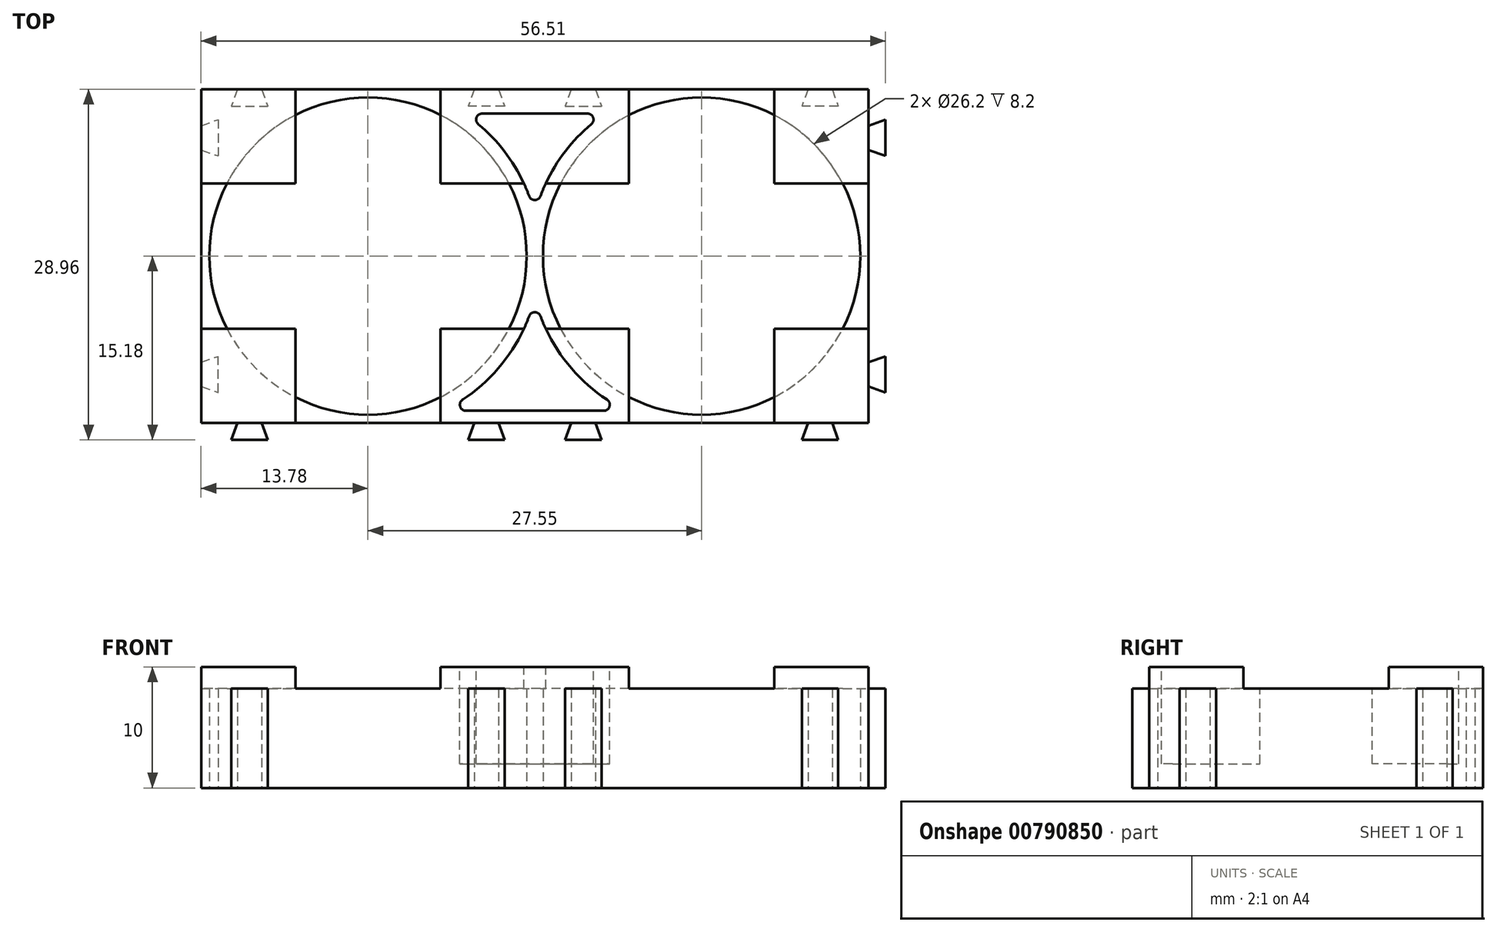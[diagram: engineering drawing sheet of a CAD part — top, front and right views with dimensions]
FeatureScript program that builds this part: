
annotation { "Feature Type Name" : "Feature", "Feature Type Description" : "" }
export const myFeature = defineFeature(function(context is Context, id is Id, definition is map)
    precondition{}
    {
        {
            var Q0;
            Q0=qCreatedBy(makeId("Top.planeOp"),FACE);
            var sketch = newSketch(context, id + "F0", { "sketchPlane" : qUnion([Q0])});
            skLineSegment(sketch, "E0.bottom", {"start": v(13.77, 13.78) * mm, "end": v(-13.77, 13.78) * mm});
            skLineSegment(sketch, "E0.top", {"start": v(13.78, -13.78) * mm, "end": v(-13.78, -13.78) * mm});
            skLineSegment(sketch, "E0.left", {"start": v(13.78, 13.78) * mm, "end": v(13.78, -13.78) * mm});
            skLineSegment(sketch, "E0.right", {"start": v(-13.78, 13.78) * mm, "end": v(-13.78, -13.78) * mm});
            skPoint(sketch, "E0.middle", {"position": v(0, 0) * mm});
            skCircle(sketch, "E1", {"center": v(0, 0) * mm, "radius": 13.1 * mm});
            skLineSegment(sketch, "E2", {"start": v(-11.28, 12.38) * mm, "end": v(-8.28, 12.38) * mm});
            skLineSegment(sketch, "E3", {"start": v(0, -13.78) * mm, "end": v(0, 13.78) * mm});
            skLineSegment(sketch, "E4", {"start": v(13.78, 0) * mm, "end": v(-13.78, 0) * mm});
            skLineSegment(sketch, "E5", {"start": v(-13.77, 13.78) * mm, "end": v(13.77, -13.78) * mm});
            skLineSegment(sketch, "E6", {"start": v(-9.78, 12.38) * mm, "end": v(-9.78, 13.78) * mm});
            skLineSegment(sketch, "E7", {"start": v(-9.78, 13.78) * mm, "end": v(-8.78, 13.78) * mm});
            skLineSegment(sketch, "E8", {"start": v(-8.78, 13.78) * mm, "end": v(-8.28, 12.38) * mm});
            skLineSegment(sketch, "E9.MirrorCS", {"start": v(-10.77, 13.78) * mm, "end": v(-11.28, 12.38) * mm});
            skLineSegment(sketch, "E10.MirrorCS", {"start": v(10.77, 13.78) * mm, "end": v(11.28, 12.38) * mm});
            skLineSegment(sketch, "E11.MirrorCS", {"start": v(11.28, 12.38) * mm, "end": v(8.28, 12.38) * mm});
            skLineSegment(sketch, "E12.MirrorCS", {"start": v(8.78, 13.78) * mm, "end": v(8.28, 12.38) * mm});
            skLineSegment(sketch, "E13.MirrorCS", {"start": v(-13.77, 10.78) * mm, "end": v(-12.37, 11.28) * mm});
            skLineSegment(sketch, "E14.MirrorCS", {"start": v(-12.37, 11.28) * mm, "end": v(-12.37, 8.28) * mm});
            skLineSegment(sketch, "E15.MirrorCS", {"start": v(-13.78, 8.78) * mm, "end": v(-12.37, 8.28) * mm});
            skLineSegment(sketch, "E16.MirrorCS", {"start": v(-13.77, -8.78) * mm, "end": v(-12.38, -8.28) * mm});
            skLineSegment(sketch, "E17.MirrorCS", {"start": v(-12.37, -11.27) * mm, "end": v(-12.37, -8.28) * mm});
            skLineSegment(sketch, "E18.MirrorCS", {"start": v(-13.78, -10.77) * mm, "end": v(-12.38, -11.27) * mm});
            skLineSegment(sketch, "E19", {"start": v(-11.28, -15.18) * mm, "end": v(-8.27, -15.18) * mm});
            skLineSegment(sketch, "E20", {"start": v(-10.77, -13.78) * mm, "end": v(-8.78, -13.78) * mm});
            skLineSegment(sketch, "E21", {"start": v(-10.77, -13.78) * mm, "end": v(-11.28, -15.18) * mm});
            skLineSegment(sketch, "E22", {"start": v(-8.78, -13.78) * mm, "end": v(-8.27, -15.17) * mm});
            skLineSegment(sketch, "E23.MirrorCS", {"start": v(8.78, -13.78) * mm, "end": v(8.27, -15.17) * mm});
            skLineSegment(sketch, "E24.MirrorCS", {"start": v(11.28, -15.18) * mm, "end": v(8.27, -15.18) * mm});
            skLineSegment(sketch, "E25.MirrorCS", {"start": v(10.77, -13.78) * mm, "end": v(11.28, -15.18) * mm});
            skLineSegment(sketch, "E26.MirrorCS", {"start": v(13.78, -10.77) * mm, "end": v(15.18, -11.28) * mm});
            skLineSegment(sketch, "E27.MirrorCS", {"start": v(15.18, -11.28) * mm, "end": v(15.18, -8.27) * mm});
            skLineSegment(sketch, "E28.MirrorCS", {"start": v(13.78, -8.78) * mm, "end": v(15.17, -8.27) * mm});
            skLineSegment(sketch, "E29.MirrorCS", {"start": v(13.78, 8.78) * mm, "end": v(15.18, 8.27) * mm});
            skLineSegment(sketch, "E30.MirrorCS", {"start": v(15.18, 11.27) * mm, "end": v(15.18, 8.27) * mm});
            skLineSegment(sketch, "E31.MirrorCS", {"start": v(13.78, 10.77) * mm, "end": v(15.18, 11.27) * mm});
            skLineSegment(sketch, "E32.1.0.0", {"start": v(38.82, -15.18) * mm, "end": v(35.82, -15.18) * mm});
            skLineSegment(sketch, "E32.1.0.1", {"start": v(41.33, 13.78) * mm, "end": v(13.78, 13.78) * mm});
            skLineSegment(sketch, "E32.1.0.2", {"start": v(41.33, -13.78) * mm, "end": v(13.78, -13.78) * mm});
            skLineSegment(sketch, "E32.1.0.3", {"start": v(41.33, 13.78) * mm, "end": v(41.33, -13.78) * mm});
            skLineSegment(sketch, "E32.1.0.4", {"start": v(13.77, 13.78) * mm, "end": v(13.77, -13.78) * mm});
            skPoint(sketch, "E32.1.0.5", {"position": v(27.55, 0) * mm});
            skLineSegment(sketch, "E32.1.0.6", {"start": v(27.55, -13.78) * mm, "end": v(27.55, 13.78) * mm});
            skLineSegment(sketch, "E32.1.0.8", {"start": v(16.28, -15.18) * mm, "end": v(19.28, -15.18) * mm});
            skLineSegment(sketch, "E32.1.0.9", {"start": v(41.33, 0) * mm, "end": v(13.78, 0) * mm});
            skLineSegment(sketch, "E32.1.0.10", {"start": v(13.78, 13.78) * mm, "end": v(41.33, -13.77) * mm});
            skLineSegment(sketch, "E32.1.0.12", {"start": v(15.18, -11.27) * mm, "end": v(15.18, -8.28) * mm});
            skCircle(sketch, "E32.1.0.13", {"center": v(27.55, 0) * mm, "radius": 13.1 * mm});
            skLineSegment(sketch, "E32.1.0.14", {"start": v(15.18, 11.28) * mm, "end": v(15.18, 8.28) * mm});
            skLineSegment(sketch, "E32.1.0.15", {"start": v(38.82, 12.37) * mm, "end": v(35.83, 12.37) * mm});
            skLineSegment(sketch, "E32.1.0.16", {"start": v(38.32, -13.77) * mm, "end": v(38.83, -15.17) * mm});
            skLineSegment(sketch, "E32.1.0.17", {"start": v(36.33, -13.78) * mm, "end": v(35.83, -15.18) * mm});
            skLineSegment(sketch, "E32.1.0.18", {"start": v(16.28, 12.38) * mm, "end": v(19.27, 12.38) * mm});
            skLineSegment(sketch, "E32.1.0.19", {"start": v(13.77, -10.77) * mm, "end": v(15.18, -11.27) * mm});
            skLineSegment(sketch, "E32.1.0.20", {"start": v(17.77, 12.38) * mm, "end": v(17.77, 13.78) * mm});
            skLineSegment(sketch, "E32.1.0.21", {"start": v(13.78, -8.78) * mm, "end": v(15.18, -8.28) * mm});
            skLineSegment(sketch, "E32.1.0.22", {"start": v(13.78, 8.78) * mm, "end": v(15.18, 8.28) * mm});
            skLineSegment(sketch, "E32.1.0.23", {"start": v(38.32, 13.78) * mm, "end": v(38.82, 12.38) * mm});
            skLineSegment(sketch, "E32.1.0.24", {"start": v(13.78, 10.78) * mm, "end": v(15.18, 11.28) * mm});
            skLineSegment(sketch, "E32.1.0.25", {"start": v(36.33, 13.78) * mm, "end": v(35.83, 12.38) * mm});
            skLineSegment(sketch, "E32.1.0.26", {"start": v(18.77, -13.78) * mm, "end": v(19.28, -15.18) * mm});
            skLineSegment(sketch, "E32.1.0.27", {"start": v(16.78, -13.78) * mm, "end": v(16.28, -15.18) * mm});
            skLineSegment(sketch, "E32.1.0.28", {"start": v(16.78, -13.78) * mm, "end": v(18.77, -13.78) * mm});
            skLineSegment(sketch, "E32.1.0.29", {"start": v(17.77, 13.78) * mm, "end": v(18.77, 13.78) * mm});
            skLineSegment(sketch, "E32.1.0.30", {"start": v(18.77, 13.78) * mm, "end": v(19.27, 12.38) * mm});
            skLineSegment(sketch, "E32.1.0.31", {"start": v(16.78, 13.78) * mm, "end": v(16.27, 12.38) * mm});
            skLineSegment(sketch, "E32.1.0.32", {"start": v(42.73, 11.27) * mm, "end": v(42.73, 8.27) * mm});
            skLineSegment(sketch, "E32.1.0.33", {"start": v(41.33, 10.77) * mm, "end": v(42.73, 11.27) * mm});
            skLineSegment(sketch, "E32.1.0.34", {"start": v(41.33, 8.78) * mm, "end": v(42.73, 8.27) * mm});
            skLineSegment(sketch, "E32.1.0.35", {"start": v(41.33, -8.78) * mm, "end": v(42.73, -8.27) * mm});
            skLineSegment(sketch, "E32.1.0.36", {"start": v(42.73, -11.28) * mm, "end": v(42.73, -8.27) * mm});
            skLineSegment(sketch, "E32.1.0.37", {"start": v(41.33, -10.77) * mm, "end": v(42.73, -11.27) * mm});
            skLineSegment(sketch, "E32.direction1", {"start": v(-13.78, -13.78) * mm, "end": v(13.78, -13.78) * mm, "construction": true});
            skSolve(sketch);
        }
        {
            var Q0;
            {var subQ4=sQuery(id+"F0.wireOp",EDGE,"E10.MirrorCS");Q0=makeQuery(id+"F0.imprint","IMPRINT",FACE,{"disambiguationData":[TD([[makeQuery(id+"F0.imprint","IMPRINT",EDGE,{"derivedFrom":subQ4}),1.0]])]});}
            var Q1;
            {var subQ0=sQuery(id+"F0.wireOp",EDGE,"E29.MirrorCS");Q1=makeQuery(id+"F0.imprint","IMPRINT",FACE,{"disambiguationData":[TD([[makeQuery(id+"F0.imprint","IMPRINT",EDGE,{"derivedFrom":subQ0}),1.0]])]});}
            var Q2;
            {var subQ0=sQuery(id+"F0.wireOp",EDGE,"E26.MirrorCS");Q2=makeQuery(id+"F0.imprint","IMPRINT",FACE,{"disambiguationData":[TD([[makeQuery(id+"F0.imprint","IMPRINT",EDGE,{"derivedFrom":subQ0}),1.0]])]});}
            var Q3;
            {var subQ0=sQuery(id+"F0.wireOp",EDGE,"E4");var subQ5=sQuery(id+"F0.wireOp",EDGE,"E0.left");var subQ9=makeQuery(id+"F0.imprint","INTERSECT",VERTEX,{"derivedFrom":[subQ5,subQ0]});Q3=makeQuery(id+"F0.imprint","IMPRINT",FACE,{"disambiguationData":[TD([[makeQuery(id+"F0.imprint","IMPRINT",EDGE,{"disambiguationData":[TD([[subQ9,-1.0]])],"derivedFrom":subQ5}),-1.0]])]});}
            var Q4;
            {var subQ1=sQuery(id+"F0.wireOp",EDGE,"E0.top");var subQ3=makeQuery(id+"F0.imprint","INTERSECT",VERTEX,{"derivedFrom":[subQ1,sQuery(id+"F0.wireOp",EDGE,"E23.MirrorCS")]});Q4=makeQuery(id+"F0.imprint","IMPRINT",FACE,{"disambiguationData":[TD([[makeQuery(id+"F0.imprint","IMPRINT",EDGE,{"disambiguationData":[TD([[subQ3,1.0]])],"derivedFrom":subQ1}),-1.0]])]});}
            var Q5;
            {var subQ0=sQuery(id+"F0.wireOp",EDGE,"E23.MirrorCS");Q5=makeQuery(id+"F0.imprint","IMPRINT",FACE,{"disambiguationData":[TD([[makeQuery(id+"F0.imprint","IMPRINT",EDGE,{"derivedFrom":subQ0}),1.0]])]});}
            var Q6;
            {var subQ11=sQuery(id+"F0.wireOp",EDGE,"E16.MirrorCS");Q6=makeQuery(id+"F0.imprint","IMPRINT",FACE,{"disambiguationData":[TD([[makeQuery(id+"F0.imprint","IMPRINT",EDGE,{"derivedFrom":subQ11}),1.0]])]});}
            var Q7;
            Q7=makeQuery(id+"F0.imprint","IMPRINT",FACE,{"disambiguationData":[TD([[makeQuery(id+"F0.imprint","IMPRINT",EDGE,{"derivedFrom":sQuery(id+"F0.wireOp",EDGE,"E19")}),1.0]])]});
            var Q8;
            {var subQ9=sQuery(id+"F0.wireOp",EDGE,"E13.MirrorCS");Q8=makeQuery(id+"F0.imprint","IMPRINT",FACE,{"disambiguationData":[TD([[makeQuery(id+"F0.imprint","IMPRINT",EDGE,{"derivedFrom":subQ9}),1.0]])]});}
            var Q9;
            {var subQ11=sQuery(id+"F0.wireOp",EDGE,"E8");Q9=makeQuery(id+"F0.imprint","IMPRINT",FACE,{"disambiguationData":[TD([[makeQuery(id+"F0.imprint","IMPRINT",EDGE,{"derivedFrom":subQ11}),1.0]])]});}
            var Q10;
            {var subQ1=sQuery(id+"F0.wireOp",EDGE,"E4");var subQ4=sQuery(id+"F0.wireOp",EDGE,"E1");var subQ5=makeQuery(id+"F0.imprint","INTERSECT",VERTEX,{"disambiguationData":[OD(0.0)],"derivedFrom":[subQ4,subQ1]});Q10=makeQuery(id+"F0.imprint","IMPRINT",FACE,{"disambiguationData":[TD([[makeQuery(id+"F0.imprint","IMPRINT",EDGE,{"disambiguationData":[TD([[subQ5,1.0]])],"derivedFrom":subQ4}),-1.0]])]});}
            var Q11;
            Q11=makeQuery(id+"F0.imprint","IMPRINT",FACE,{"disambiguationData":[TD([[makeQuery(id+"F0.imprint","IMPRINT",EDGE,{"derivedFrom":sQuery(id+"F0.wireOp",EDGE,"E32.1.0.12")}),-1.0]])]});
            var Q12;
            Q12=makeQuery(id+"F0.imprint","IMPRINT",FACE,{"disambiguationData":[TD([[makeQuery(id+"F0.imprint","IMPRINT",EDGE,{"derivedFrom":sQuery(id+"F0.wireOp",EDGE,"E32.1.0.12")}),1.0]])]});
            var Q13;
            Q13=makeQuery(id+"F0.imprint","IMPRINT",FACE,{"disambiguationData":[TD([[makeQuery(id+"F0.imprint","IMPRINT",EDGE,{"derivedFrom":sQuery(id+"F0.wireOp",EDGE,"E32.1.0.14")}),-1.0]])]});
            var Q14;
            Q14=makeQuery(id+"F0.imprint","IMPRINT",FACE,{"disambiguationData":[TD([[makeQuery(id+"F0.imprint","IMPRINT",EDGE,{"derivedFrom":sQuery(id+"F0.wireOp",EDGE,"E32.1.0.14")}),1.0]])]});
            var Q15;
            {var subQ13=sQuery(id+"F0.wireOp",EDGE,"E32.1.0.30");Q15=makeQuery(id+"F0.imprint","IMPRINT",FACE,{"disambiguationData":[TD([[makeQuery(id+"F0.imprint","IMPRINT",EDGE,{"derivedFrom":subQ13}),1.0]])]});}
            var Q16;
            {var subQ1=sQuery(id+"F0.wireOp",EDGE,"E0.bottom");var subQ3=sQuery(id+"F0.wireOp",EDGE,"E32.1.0.7");var subQ4=makeQuery(id+"F0.imprint","INTERSECT",VERTEX,{"derivedFrom":[subQ1,subQ3]});Q16=makeQuery(id+"F0.imprint","IMPRINT",FACE,{"disambiguationData":[TD([[makeQuery(id+"F0.imprint","IMPRINT",EDGE,{"disambiguationData":[TD([[subQ4,1.0]])],"derivedFrom":subQ3}),-1.0]])]});}
            var Q17;
            {var subQ1=sQuery(id+"F0.wireOp",EDGE,"E32.1.0.4");var subQ3=sQuery(id+"F0.wireOp",EDGE,"E32.1.0.7");var subQ4=makeQuery(id+"F0.imprint","INTERSECT",VERTEX,{"derivedFrom":[subQ1,subQ3]});Q17=makeQuery(id+"F0.imprint","IMPRINT",FACE,{"disambiguationData":[TD([[makeQuery(id+"F0.imprint","IMPRINT",EDGE,{"disambiguationData":[TD([[subQ4,1.0]])],"derivedFrom":subQ3}),-1.0]])]});}
            var Q18;
            {var subQ1=sQuery(id+"F0.wireOp",EDGE,"E32.1.0.1");var subQ3=sQuery(id+"F0.wireOp",EDGE,"E32.1.0.7");var subQ4=makeQuery(id+"F0.imprint","INTERSECT",VERTEX,{"derivedFrom":[subQ1,subQ3]});Q18=makeQuery(id+"F0.imprint","IMPRINT",FACE,{"disambiguationData":[TD([[makeQuery(id+"F0.imprint","IMPRINT",EDGE,{"disambiguationData":[TD([[subQ4,-1.0]])],"derivedFrom":subQ3}),-1.0]])]});}
            var Q19;
            Q19=makeQuery(id+"F0.imprint","IMPRINT",FACE,{"disambiguationData":[TD([[makeQuery(id+"F0.imprint","IMPRINT",EDGE,{"derivedFrom":sQuery(id+"F0.wireOp",EDGE,"E32.1.0.15")}),1.0]])]});
            var Q20;
            Q20=makeQuery(id+"F0.imprint","IMPRINT",FACE,{"disambiguationData":[TD([[makeQuery(id+"F0.imprint","IMPRINT",EDGE,{"derivedFrom":sQuery(id+"F0.wireOp",EDGE,"E32.1.0.32")}),-1.0]])]});
            var Q21;
            Q21=makeQuery(id+"F0.imprint","IMPRINT",FACE,{"disambiguationData":[TD([[makeQuery(id+"F0.imprint","IMPRINT",EDGE,{"derivedFrom":sQuery(id+"F0.wireOp",EDGE,"E32.1.0.8")}),1.0]])]});
            var Q22;
            Q22=makeQuery(id+"F0.imprint","IMPRINT",FACE,{"disambiguationData":[TD([[makeQuery(id+"F0.imprint","IMPRINT",EDGE,{"derivedFrom":sQuery(id+"F0.wireOp",EDGE,"E32.1.0.0")}),-1.0]])]});
            var Q23;
            {var subQ0=sQuery(id+"F0.wireOp",EDGE,"E32.1.0.35");Q23=makeQuery(id+"F0.imprint","IMPRINT",FACE,{"disambiguationData":[TD([[makeQuery(id+"F0.imprint","IMPRINT",EDGE,{"derivedFrom":subQ0}),-1.0]])]});}
            var Q24;
            {var subQ1=sQuery(id+"F0.wireOp",EDGE,"E32.1.0.3");var subQ5=sQuery(id+"F0.wireOp",EDGE,"E32.1.0.9");var subQ6=makeQuery(id+"F0.imprint","INTERSECT",VERTEX,{"derivedFrom":[subQ1,subQ5]});Q24=makeQuery(id+"F0.imprint","IMPRINT",FACE,{"disambiguationData":[TD([[makeQuery(id+"F0.imprint","IMPRINT",EDGE,{"disambiguationData":[TD([[subQ6,-1.0]])],"derivedFrom":subQ1}),-1.0]])]});}
            var Q25;
            {var subQ1=sQuery(id+"F0.wireOp",EDGE,"E32.1.0.2");var subQ4=makeQuery(id+"F0.imprint","INTERSECT",VERTEX,{"derivedFrom":[subQ1,sQuery(id+"F0.wireOp",EDGE,"E32.1.0.16")]});Q25=makeQuery(id+"F0.imprint","IMPRINT",FACE,{"disambiguationData":[TD([[makeQuery(id+"F0.imprint","IMPRINT",EDGE,{"disambiguationData":[TD([[subQ4,-1.0]])],"derivedFrom":subQ1}),-1.0]])]});}
            extrude(context, id + "F1", {"entities" : qUnion([Q0, Q1, Q2, Q3, Q4, Q5, Q6, Q7, Q8, Q9, Q10, Q11, Q12, Q13, Q14, Q15, Q16, Q17, Q18, Q19, Q20, Q21, Q22, Q23, Q24, Q25]), "depth" : (10 - 1.8) * mm, "offsetDistance" : 25 * mm});
        }
        {
            var Q0;
            Q0=makeQuery(id+"F1.opExtrude","CAP_FACE",FACE,{"disambiguationData":[OSD([sQuery(id+"F0.wireOp",EDGE,"E0.bottom"),sQuery(id+"F0.wireOp",EDGE,"E0.top"),sQuery(id+"F0.wireOp",EDGE,"E0.left"),sQuery(id+"F0.wireOp",EDGE,"E0.right"),sQuery(id+"F0.wireOp",EDGE,"E1"),sQuery(id+"F0.wireOp",EDGE,"E2"),sQuery(id+"F0.wireOp",EDGE,"E8"),sQuery(id+"F0.wireOp",EDGE,"E9.MirrorCS"),sQuery(id+"F0.wireOp",EDGE,"E10.MirrorCS"),sQuery(id+"F0.wireOp",EDGE,"E11.MirrorCS"),sQuery(id+"F0.wireOp",EDGE,"E12.MirrorCS"),sQuery(id+"F0.wireOp",EDGE,"E13.MirrorCS"),sQuery(id+"F0.wireOp",EDGE,"E14.MirrorCS"),sQuery(id+"F0.wireOp",EDGE,"E15.MirrorCS"),sQuery(id+"F0.wireOp",EDGE,"E16.MirrorCS"),sQuery(id+"F0.wireOp",EDGE,"E17.MirrorCS"),sQuery(id+"F0.wireOp",EDGE,"E18.MirrorCS"),sQuery(id+"F0.wireOp",EDGE,"E19"),sQuery(id+"F0.wireOp",EDGE,"E21"),sQuery(id+"F0.wireOp",EDGE,"E22"),sQuery(id+"F0.wireOp",EDGE,"E23.MirrorCS"),sQuery(id+"F0.wireOp",EDGE,"E24.MirrorCS"),sQuery(id+"F0.wireOp",EDGE,"E25.MirrorCS"),sQuery(id+"F0.wireOp",EDGE,"E26.MirrorCS"),sQuery(id+"F0.wireOp",EDGE,"E27.MirrorCS"),sQuery(id+"F0.wireOp",EDGE,"E28.MirrorCS"),sQuery(id+"F0.wireOp",EDGE,"E29.MirrorCS"),sQuery(id+"F0.wireOp",EDGE,"E30.MirrorCS"),sQuery(id+"F0.wireOp",EDGE,"E31.MirrorCS")])],"isStart":false});
            var sketch = newSketch(context, id + "F2", { "sketchPlane" : qUnion([Q0])});
            skLineSegment(sketch, "E33", {"start": v(13.78, -13.78) * mm, "end": v(-13.78, 13.78) * mm});
            skLineSegment(sketch, "E34", {"start": v(13.78, 13.77) * mm, "end": v(-13.77, -13.78) * mm});
            skLineSegment(sketch, "E35", {"start": v(0, 0) * mm, "end": v(0, -13.77) * mm});
            skLineSegment(sketch, "E36", {"start": v(0, -13.78) * mm, "end": v(6, -13.78) * mm});
            skLineSegment(sketch, "E37", {"start": v(6, -13.78) * mm, "end": v(6, -6) * mm});
            skLineSegment(sketch, "E38", {"start": v(6, -6) * mm, "end": v(13.78, -6) * mm});
            skLineSegment(sketch, "E39", {"start": v(6, 6) * mm, "end": v(6, 13.77) * mm});
            skLineSegment(sketch, "E40", {"start": v(6, 6) * mm, "end": v(13.78, 6) * mm});
            skLineSegment(sketch, "E41", {"start": v(6, 13.77) * mm, "end": v(13.78, 13.77) * mm});
            skLineSegment(sketch, "E42", {"start": v(13.78, 6) * mm, "end": v(13.78, 13.77) * mm});
            skLineSegment(sketch, "E43", {"start": v(13.78, -6) * mm, "end": v(13.78, -13.78) * mm});
            skLineSegment(sketch, "E44", {"start": v(6, -13.78) * mm, "end": v(13.78, -13.78) * mm});
            skLineSegment(sketch, "E45", {"start": v(-6, 6) * mm, "end": v(-13.78, 6) * mm});
            skLineSegment(sketch, "E46", {"start": v(-6, 6) * mm, "end": v(-6, 13.78) * mm});
            skLineSegment(sketch, "E47", {"start": v(-6, 13.78) * mm, "end": v(-13.78, 13.78) * mm});
            skLineSegment(sketch, "E48", {"start": v(-13.78, 13.78) * mm, "end": v(-13.78, 6) * mm});
            skLineSegment(sketch, "E49", {"start": v(-6, -6) * mm, "end": v(-13.78, -6) * mm});
            skLineSegment(sketch, "E50", {"start": v(-6, -6) * mm, "end": v(-6, -13.78) * mm});
            skLineSegment(sketch, "E51", {"start": v(-6, -13.78) * mm, "end": v(-13.78, -13.78) * mm});
            skLineSegment(sketch, "E52", {"start": v(-13.78, -13.78) * mm, "end": v(-13.78, -6) * mm});
            skLineSegment(sketch, "E53.1.0.0", {"start": v(13.78, 13.78) * mm, "end": v(13.78, 6) * mm});
            skLineSegment(sketch, "E53.1.0.1", {"start": v(21.55, 13.78) * mm, "end": v(13.77, 13.78) * mm});
            skLineSegment(sketch, "E53.1.0.2", {"start": v(21.55, 6) * mm, "end": v(21.55, 13.78) * mm});
            skLineSegment(sketch, "E53.1.0.3", {"start": v(21.55, 6) * mm, "end": v(13.78, 6) * mm});
            skLineSegment(sketch, "E53.1.0.4", {"start": v(33.55, 6) * mm, "end": v(33.55, 13.78) * mm});
            skLineSegment(sketch, "E53.1.0.5", {"start": v(33.55, 13.78) * mm, "end": v(41.33, 13.78) * mm});
            skLineSegment(sketch, "E53.1.0.6", {"start": v(41.33, 6) * mm, "end": v(41.33, 13.78) * mm});
            skLineSegment(sketch, "E53.1.0.7", {"start": v(33.55, 6) * mm, "end": v(41.33, 6) * mm});
            skLineSegment(sketch, "E53.1.0.8", {"start": v(33.55, -6) * mm, "end": v(41.33, -6) * mm});
            skLineSegment(sketch, "E53.1.0.9", {"start": v(33.55, -13.78) * mm, "end": v(33.55, -6) * mm});
            skLineSegment(sketch, "E53.1.0.10", {"start": v(33.55, -13.78) * mm, "end": v(41.33, -13.78) * mm});
            skLineSegment(sketch, "E53.1.0.11", {"start": v(41.33, -6) * mm, "end": v(41.33, -13.78) * mm});
            skLineSegment(sketch, "E53.1.0.12", {"start": v(21.55, -6) * mm, "end": v(21.55, -13.78) * mm});
            skLineSegment(sketch, "E53.1.0.13", {"start": v(21.55, -6) * mm, "end": v(13.78, -6) * mm});
            skLineSegment(sketch, "E53.1.0.14", {"start": v(13.78, -13.78) * mm, "end": v(13.78, -6) * mm});
            skLineSegment(sketch, "E53.1.0.15", {"start": v(21.55, -13.77) * mm, "end": v(13.77, -13.77) * mm});
            skLineSegment(sketch, "E53.direction1", {"start": v(-13.78, 6) * mm, "end": v(13.78, 6) * mm, "construction": true});
            skSolve(sketch);
        }
        {
            var Q0;
            {var subQ1=makeQuery(id+"F1.opExtrude","CAP_EDGE",EDGE,{"disambiguationData":[OSD([sQuery(id+"F0.wireOp",EDGE,"E10.MirrorCS")])],"isStart":false});Q0=makeQuery(id+"F2.imprint","IMPRINT",FACE,{"disambiguationData":[TD([[makeQuery(id+"F2.imprint","IMPRINT",EDGE,{"derivedFrom":subQ1}),-1.0]])]});}
            var Q1;
            Q1=makeQuery(id+"F2.imprint","IMPRINT",FACE,{"disambiguationData":[TD([[makeQuery(id+"F2.imprint","IMPRINT",EDGE,{"derivedFrom":makeQuery(id+"F1.opExtrude","CAP_EDGE",EDGE,{"disambiguationData":[OSD([sQuery(id+"F0.wireOp",EDGE,"E2")])],"isStart":false})}),1.0]])]});
            var Q2;
            {var subQ1=makeQuery(id+"F1.opExtrude","CAP_EDGE",EDGE,{"disambiguationData":[OSD([sQuery(id+"F0.wireOp",EDGE,"E13.MirrorCS")])],"isStart":false});Q2=makeQuery(id+"F2.imprint","IMPRINT",FACE,{"disambiguationData":[TD([[makeQuery(id+"F2.imprint","IMPRINT",EDGE,{"derivedFrom":subQ1}),-1.0]])]});}
            var Q3;
            {var subQ1=makeQuery(id+"F1.opExtrude","CAP_EDGE",EDGE,{"disambiguationData":[OSD([sQuery(id+"F0.wireOp",EDGE,"E16.MirrorCS")])],"isStart":false});Q3=makeQuery(id+"F2.imprint","IMPRINT",FACE,{"disambiguationData":[TD([[makeQuery(id+"F2.imprint","IMPRINT",EDGE,{"derivedFrom":subQ1}),-1.0]])]});}
            var Q4;
            Q4=makeQuery(id+"F2.imprint","IMPRINT",FACE,{"disambiguationData":[TD([[makeQuery(id+"F2.imprint","IMPRINT",EDGE,{"derivedFrom":makeQuery(id+"F1.opExtrude","CAP_EDGE",EDGE,{"disambiguationData":[OSD([sQuery(id+"F0.wireOp",EDGE,"E32.1.0.18")])],"isStart":false})}),1.0]])]});
            var Q5;
            Q5=makeQuery(id+"F2.imprint","IMPRINT",FACE,{"disambiguationData":[TD([[makeQuery(id+"F2.imprint","IMPRINT",EDGE,{"derivedFrom":makeQuery(id+"F1.opExtrude","CAP_EDGE",EDGE,{"disambiguationData":[OSD([sQuery(id+"F0.wireOp",EDGE,"E32.1.0.15")])],"isStart":false})}),-1.0]])]});
            var Q6;
            {var subQ0=sQuery(id+"F2.wireOp",EDGE,"E53.1.0.3");var subQ1=sQuery(id+"F2.wireOp",EDGE,"E53.1.0.2");var subQ2=makeQuery(id+"F2.imprint","INTERSECT",VERTEX,{"derivedFrom":[subQ1,subQ0]});Q6=makeQuery(id+"F2.imprint","IMPRINT",FACE,{"disambiguationData":[TD([[makeQuery(id+"F2.imprint","IMPRINT",EDGE,{"disambiguationData":[TD([[subQ2,-1.0]])],"derivedFrom":subQ1}),1.0]])]});}
            var Q7;
            {var subQ0=sQuery(id+"F2.wireOp",EDGE,"E53.1.0.7");var subQ1=sQuery(id+"F2.wireOp",EDGE,"E53.1.0.4");var subQ2=makeQuery(id+"F2.imprint","INTERSECT",VERTEX,{"derivedFrom":[subQ1,subQ0]});Q7=makeQuery(id+"F2.imprint","IMPRINT",FACE,{"disambiguationData":[TD([[makeQuery(id+"F2.imprint","IMPRINT",EDGE,{"disambiguationData":[TD([[subQ2,-1.0]])],"derivedFrom":subQ1}),-1.0]])]});}
            var Q8;
            {var subQ0=sQuery(id+"F2.wireOp",EDGE,"E53.1.0.9");var subQ1=sQuery(id+"F2.wireOp",EDGE,"E53.1.0.8");var subQ2=makeQuery(id+"F2.imprint","INTERSECT",VERTEX,{"derivedFrom":[subQ1,subQ0]});Q8=makeQuery(id+"F2.imprint","IMPRINT",FACE,{"disambiguationData":[TD([[makeQuery(id+"F2.imprint","IMPRINT",EDGE,{"disambiguationData":[TD([[subQ2,-1.0]])],"derivedFrom":subQ1}),-1.0]])]});}
            var Q9;
            {var subQ0=sQuery(id+"F2.wireOp",EDGE,"E53.1.0.13");var subQ1=sQuery(id+"F2.wireOp",EDGE,"E53.1.0.12");var subQ2=makeQuery(id+"F2.imprint","INTERSECT",VERTEX,{"derivedFrom":[subQ1,subQ0]});Q9=makeQuery(id+"F2.imprint","IMPRINT",FACE,{"disambiguationData":[TD([[makeQuery(id+"F2.imprint","IMPRINT",EDGE,{"disambiguationData":[TD([[subQ2,-1.0]])],"derivedFrom":subQ1}),-1.0]])]});}
            var Q10;
            {var subQ1=sQuery(id+"F2.wireOp",EDGE,"E33");var subQ3=makeQuery(id+"F1.opExtrude","CAP_EDGE",EDGE,{"disambiguationData":[OSD([sQuery(id+"F0.wireOp",EDGE,"E1")])],"isStart":false});var subQ4=makeQuery(id+"F2.imprint","INTERSECT",VERTEX,{"disambiguationData":[OD(0.0)],"derivedFrom":[subQ3,subQ1]});Q10=makeQuery(id+"F2.imprint","IMPRINT",FACE,{"disambiguationData":[TD([[makeQuery(id+"F2.imprint","IMPRINT",EDGE,{"disambiguationData":[TD([[subQ4,1.0]])],"derivedFrom":subQ3}),1.0]])]});}
            var Q11;
            {var subQ1=sQuery(id+"F2.wireOp",EDGE,"E33");var subQ3=makeQuery(id+"F1.opExtrude","CAP_EDGE",EDGE,{"disambiguationData":[OSD([sQuery(id+"F0.wireOp",EDGE,"E1")])],"isStart":false});var subQ4=makeQuery(id+"F2.imprint","INTERSECT",VERTEX,{"disambiguationData":[OD(0.0)],"derivedFrom":[subQ3,subQ1]});Q11=makeQuery(id+"F2.imprint","IMPRINT",FACE,{"disambiguationData":[TD([[makeQuery(id+"F2.imprint","IMPRINT",EDGE,{"disambiguationData":[TD([[subQ4,-1.0]])],"derivedFrom":subQ3}),1.0]])]});}
            var Q12;
            {var subQ1=sQuery(id+"F2.wireOp",EDGE,"E33");var subQ3=makeQuery(id+"F1.opExtrude","CAP_EDGE",EDGE,{"disambiguationData":[OSD([sQuery(id+"F0.wireOp",EDGE,"E1")])],"isStart":false});var subQ4=makeQuery(id+"F2.imprint","INTERSECT",VERTEX,{"disambiguationData":[OD(1.0)],"derivedFrom":[subQ3,subQ1]});Q12=makeQuery(id+"F2.imprint","IMPRINT",FACE,{"disambiguationData":[TD([[makeQuery(id+"F2.imprint","IMPRINT",EDGE,{"disambiguationData":[TD([[subQ4,-1.0]])],"derivedFrom":subQ3}),1.0]])]});}
            var Q13;
            {var subQ1=sQuery(id+"F2.wireOp",EDGE,"E33");var subQ3=makeQuery(id+"F1.opExtrude","CAP_EDGE",EDGE,{"disambiguationData":[OSD([sQuery(id+"F0.wireOp",EDGE,"E1")])],"isStart":false});var subQ4=makeQuery(id+"F2.imprint","INTERSECT",VERTEX,{"disambiguationData":[OD(1.0)],"derivedFrom":[subQ3,subQ1]});Q13=makeQuery(id+"F2.imprint","IMPRINT",FACE,{"disambiguationData":[TD([[makeQuery(id+"F2.imprint","IMPRINT",EDGE,{"disambiguationData":[TD([[subQ4,1.0]])],"derivedFrom":subQ3}),1.0]])]});}
            var Q14;
            {var subQ1=sQuery(id+"F2.wireOp",EDGE,"E34");var subQ3=makeQuery(id+"F1.opExtrude","CAP_EDGE",EDGE,{"disambiguationData":[OSD([sQuery(id+"F0.wireOp",EDGE,"E1")])],"isStart":false});var subQ4=makeQuery(id+"F2.imprint","INTERSECT",VERTEX,{"disambiguationData":[OD(0.0)],"derivedFrom":[subQ3,subQ1]});Q14=makeQuery(id+"F2.imprint","IMPRINT",FACE,{"disambiguationData":[TD([[makeQuery(id+"F2.imprint","IMPRINT",EDGE,{"disambiguationData":[TD([[subQ4,-1.0]])],"derivedFrom":subQ3}),1.0]])]});}
            var Q15;
            {var subQ1=sQuery(id+"F2.wireOp",EDGE,"E34");var subQ3=makeQuery(id+"F1.opExtrude","CAP_EDGE",EDGE,{"disambiguationData":[OSD([sQuery(id+"F0.wireOp",EDGE,"E1")])],"isStart":false});var subQ4=makeQuery(id+"F2.imprint","INTERSECT",VERTEX,{"disambiguationData":[OD(0.0)],"derivedFrom":[subQ3,subQ1]});Q15=makeQuery(id+"F2.imprint","IMPRINT",FACE,{"disambiguationData":[TD([[makeQuery(id+"F2.imprint","IMPRINT",EDGE,{"disambiguationData":[TD([[subQ4,1.0]])],"derivedFrom":subQ3}),1.0]])]});}
            var Q16;
            {var subQ1=sQuery(id+"F2.wireOp",EDGE,"E34");var subQ3=makeQuery(id+"F1.opExtrude","CAP_EDGE",EDGE,{"disambiguationData":[OSD([sQuery(id+"F0.wireOp",EDGE,"E1")])],"isStart":false});var subQ4=makeQuery(id+"F2.imprint","INTERSECT",VERTEX,{"disambiguationData":[OD(1.0)],"derivedFrom":[subQ3,subQ1]});Q16=makeQuery(id+"F2.imprint","IMPRINT",FACE,{"disambiguationData":[TD([[makeQuery(id+"F2.imprint","IMPRINT",EDGE,{"disambiguationData":[TD([[subQ4,1.0]])],"derivedFrom":subQ3}),1.0]])]});}
            var Q17;
            {var subQ1=sQuery(id+"F2.wireOp",EDGE,"E34");var subQ3=makeQuery(id+"F1.opExtrude","CAP_EDGE",EDGE,{"disambiguationData":[OSD([sQuery(id+"F0.wireOp",EDGE,"E1")])],"isStart":false});var subQ4=makeQuery(id+"F2.imprint","INTERSECT",VERTEX,{"disambiguationData":[OD(1.0)],"derivedFrom":[subQ3,subQ1]});Q17=makeQuery(id+"F2.imprint","IMPRINT",FACE,{"disambiguationData":[TD([[makeQuery(id+"F2.imprint","IMPRINT",EDGE,{"disambiguationData":[TD([[subQ4,-1.0]])],"derivedFrom":subQ3}),1.0]])]});}
            var Q18;
            {var subQ0=sQuery(id+"F2.wireOp",EDGE,"E44");var subQ1=makeQuery(id+"F2.imprint","INTERSECT",VERTEX,{"derivedFrom":[makeQuery(id+"F1.opExtrude","CAP_EDGE",EDGE,{"disambiguationData":[OSD([sQuery(id+"F0.wireOp",EDGE,"E23.MirrorCS")])],"isStart":false}),subQ0]});var subQ4=makeQuery(id+"F2.imprint","INTERSECT",VERTEX,{"derivedFrom":[makeQuery(id+"F1.opExtrude","CAP_EDGE",EDGE,{"disambiguationData":[OSD([sQuery(id+"F0.wireOp",EDGE,"E25.MirrorCS")])],"isStart":false}),subQ0]});Q18=makeQuery(id+"F2.imprint","IMPRINT",FACE,{"disambiguationData":[TD([[makeQuery(id+"F2.imprint","IMPRINT",EDGE,{"disambiguationData":[TD([[subQ1,-1.0],[subQ4,1.0]])],"derivedFrom":subQ0}),1.0]])]});}
            var Q19;
            {var subQ0=sQuery(id+"F2.wireOp",EDGE,"E53.1.0.14");Q19=makeQuery(id+"F2.imprint","IMPRINT",FACE,{"disambiguationData":[TD([[makeQuery(id+"F2.imprint","IMPRINT",EDGE,{"derivedFrom":subQ0}),1.0]])]});}
            var Q20;
            {var subQ9=makeQuery(id+"F1.opExtrude","CAP_EDGE",EDGE,{"disambiguationData":[OSD([sQuery(id+"F0.wireOp",EDGE,"E13.MirrorCS")])],"isStart":false});Q20=makeQuery(id+"F2.imprint","IMPRINT",FACE,{"disambiguationData":[TD([[makeQuery(id+"F2.imprint","IMPRINT",EDGE,{"derivedFrom":subQ9}),1.0]])]});}
            var Q21;
            Q21=makeQuery(id+"F2.imprint","IMPRINT",FACE,{"disambiguationData":[TD([[makeQuery(id+"F2.imprint","IMPRINT",EDGE,{"derivedFrom":makeQuery(id+"F1.opExtrude","CAP_EDGE",EDGE,{"disambiguationData":[OSD([sQuery(id+"F0.wireOp",EDGE,"E2")])],"isStart":false})}),-1.0]])]});
            var Q22;
            {var subQ7=makeQuery(id+"F1.opExtrude","CAP_EDGE",EDGE,{"disambiguationData":[OSD([sQuery(id+"F0.wireOp",EDGE,"E10.MirrorCS")])],"isStart":false});Q22=makeQuery(id+"F2.imprint","IMPRINT",FACE,{"disambiguationData":[TD([[makeQuery(id+"F2.imprint","IMPRINT",EDGE,{"derivedFrom":subQ7}),1.0]])]});}
            var Q23;
            {var subQ0=sQuery(id+"F2.wireOp",EDGE,"E53.1.0.0");Q23=makeQuery(id+"F2.imprint","IMPRINT",FACE,{"disambiguationData":[TD([[makeQuery(id+"F2.imprint","IMPRINT",EDGE,{"derivedFrom":subQ0}),-1.0]])]});}
            var Q24;
            {var subQ4=sQuery(id+"F0.wireOp",EDGE,"E16.MirrorCS");var subQ5=makeQuery(id+"F1.opExtrude","CAP_EDGE",EDGE,{"disambiguationData":[OSD([subQ4])],"isStart":false});Q24=makeQuery(id+"F2.imprint","IMPRINT",FACE,{"disambiguationData":[TD([[makeQuery(id+"F2.imprint","IMPRINT",EDGE,{"derivedFrom":subQ5}),1.0]])]});}
            var Q25;
            {var subQ0=sQuery(id+"F2.wireOp",EDGE,"E51");var subQ11=makeQuery(id+"F2.imprint","INTERSECT",VERTEX,{"derivedFrom":[makeQuery(id+"F1.opExtrude","CAP_EDGE",EDGE,{"disambiguationData":[OSD([sQuery(id+"F0.wireOp",EDGE,"E21")])],"isStart":false}),subQ0]});Q25=makeQuery(id+"F2.imprint","IMPRINT",FACE,{"disambiguationData":[TD([[makeQuery(id+"F2.imprint","IMPRINT",EDGE,{"disambiguationData":[TD([[subQ11,1.0]])],"derivedFrom":subQ0}),-1.0]])]});}
            var Q26;
            {var subQ12=sQuery(id+"F2.wireOp",EDGE,"E53.1.0.0");Q26=makeQuery(id+"F2.imprint","IMPRINT",FACE,{"disambiguationData":[TD([[makeQuery(id+"F2.imprint","IMPRINT",EDGE,{"derivedFrom":subQ12}),1.0]])]});}
            var Q27;
            Q27=makeQuery(id+"F2.imprint","IMPRINT",FACE,{"disambiguationData":[TD([[makeQuery(id+"F2.imprint","IMPRINT",EDGE,{"derivedFrom":makeQuery(id+"F1.opExtrude","CAP_EDGE",EDGE,{"disambiguationData":[OSD([sQuery(id+"F0.wireOp",EDGE,"E32.1.0.15")])],"isStart":false})}),1.0]])]});
            var Q28;
            {var subQ0=sQuery(id+"F2.wireOp",EDGE,"E53.1.0.10");var subQ7=sQuery(id+"F2.wireOp",EDGE,"E53.1.0.11");var subQ8=makeQuery(id+"F2.imprint","INTERSECT",VERTEX,{"derivedFrom":[subQ0,subQ7]});var subQ9=makeQuery(id+"F2.imprint","INTERSECT",VERTEX,{"derivedFrom":[makeQuery(id+"F1.opExtrude","CAP_EDGE",EDGE,{"disambiguationData":[OSD([sQuery(id+"F0.wireOp",EDGE,"E32.1.0.16")])],"isStart":false}),subQ0]});Q28=makeQuery(id+"F2.imprint","IMPRINT",FACE,{"disambiguationData":[TD([[makeQuery(id+"F2.imprint","IMPRINT",EDGE,{"disambiguationData":[TD([[subQ8,-1.0],[subQ9,1.0]])],"derivedFrom":subQ0}),-1.0]])]});}
            var Q29;
            {var subQ2=sQuery(id+"F2.wireOp",EDGE,"E53.1.0.14");Q29=makeQuery(id+"F2.imprint","IMPRINT",FACE,{"disambiguationData":[TD([[makeQuery(id+"F2.imprint","IMPRINT",EDGE,{"derivedFrom":subQ2}),-1.0]])]});}
            var Q30;
            {var subQ2=sQuery(id+"F2.wireOp",EDGE,"E43");Q30=makeQuery(id+"F2.imprint","IMPRINT",FACE,{"disambiguationData":[TD([[makeQuery(id+"F2.imprint","IMPRINT",EDGE,{"derivedFrom":subQ2}),1.0]])]});}
            var Q31;
            {var subQ9=sQuery(id+"F2.wireOp",EDGE,"E42");Q31=makeQuery(id+"F2.imprint","IMPRINT",FACE,{"disambiguationData":[TD([[makeQuery(id+"F2.imprint","IMPRINT",EDGE,{"derivedFrom":subQ9}),-1.0]])]});}
            var Q32;
            {var subQ0=sQuery(id+"F2.wireOp",EDGE,"E42");Q32=makeQuery(id+"F2.imprint","IMPRINT",FACE,{"disambiguationData":[TD([[makeQuery(id+"F2.imprint","IMPRINT",EDGE,{"derivedFrom":subQ0}),1.0]])]});}
            var Q33;
            {var subQ0=sQuery(id+"F2.wireOp",EDGE,"E43");Q33=makeQuery(id+"F2.imprint","IMPRINT",FACE,{"disambiguationData":[TD([[makeQuery(id+"F2.imprint","IMPRINT",EDGE,{"derivedFrom":subQ0}),-1.0]])]});}
            extrude(context, id + "F3", {"entities" : qUnion([Q0, Q1, Q2, Q3, Q4, Q5, Q6, Q7, Q8, Q9, Q10, Q11, Q12, Q13, Q14, Q15, Q16, Q17, Q18, Q19, Q20, Q21, Q22, Q23, Q24, Q25, Q26, Q27, Q28, Q29, Q30, Q31, Q32, Q33]), "operationType" : NewBodyOperationType.ADD, "depth" : 1.8 * mm, "offsetDistance" : 25 * mm});
        }
        {
            var Q0;
            Q0=makeQuery(id+"F3.opExtrude","CAP_FACE",FACE,{"disambiguationData":[OSD([sQuery(id+"F2.wireOp",EDGE,"E39"),sQuery(id+"F2.wireOp",EDGE,"E40"),sQuery(id+"F2.wireOp",EDGE,"E41"),sQuery(id+"F2.wireOp",EDGE,"E53.1.0.1"),sQuery(id+"F2.wireOp",EDGE,"E53.1.0.2"),sQuery(id+"F2.wireOp",EDGE,"E53.1.0.3")])],"isStart":false});
            var sketch = newSketch(context, id + "F4", { "sketchPlane" : qUnion([Q0])});
            skCircle(sketch, "E54", {"center": v(0, 0) * mm, "radius": 14.2 * mm});
            skCircle(sketch, "E55", {"center": v(27.55, 0) * mm, "radius": 14.2 * mm});
            skLineSegment(sketch, "E56", {"start": v(7.94, 11.78) * mm, "end": v(19.61, 11.78) * mm});
            skLineSegment(sketch, "E57", {"start": v(6.2, -12.78) * mm, "end": v(21.35, -12.78) * mm});
            skCircle(sketch, "E58", {"center": v(9.43, 11.27) * mm, "radius": 0.5 * mm});
            skCircle(sketch, "E59", {"center": v(18.12, 11.27) * mm, "radius": 0.5 * mm});
            skCircle(sketch, "E60", {"center": v(13.77, 5.13) * mm, "radius": 0.5 * mm});
            skCircle(sketch, "E61", {"center": v(13.77, -5.13) * mm, "radius": 0.5 * mm});
            skCircle(sketch, "E62", {"center": v(8.09, -12.28) * mm, "radius": 0.5 * mm});
            skCircle(sketch, "E63", {"center": v(19.46, -12.28) * mm, "radius": 0.5 * mm});
            skSolve(sketch);
        }
        {
            var Q0;
            {var subQ1=sQuery(id+"F4.wireOp",EDGE,"E54");var subQ5=sQuery(id+"F4.wireOp",EDGE,"E62");var subQ10=makeQuery(id+"F4.imprint","INTERSECT",VERTEX,{"derivedFrom":[subQ1,subQ5]});Q0=makeQuery(id+"F4.imprint","IMPRINT",FACE,{"disambiguationData":[TD([[makeQuery(id+"F4.imprint","IMPRINT",EDGE,{"disambiguationData":[TD([[subQ10,-1.0]])],"derivedFrom":subQ1}),-1.0]])]});}
            var Q1;
            {var subQ0=sQuery(id+"F4.wireOp",EDGE,"E62");var subQ1=makeQuery(id+"F4.imprint","INTERSECT",VERTEX,{"derivedFrom":[sQuery(id+"F4.wireOp",EDGE,"E57"),subQ0]});Q1=makeQuery(id+"F4.imprint","IMPRINT",FACE,{"disambiguationData":[TD([[makeQuery(id+"F4.imprint","IMPRINT",EDGE,{"disambiguationData":[TD([[subQ1,1.0]])],"derivedFrom":subQ0}),1.0]])]});}
            var Q2;
            {var subQ0=sQuery(id+"F4.wireOp",EDGE,"E63");var subQ1=makeQuery(id+"F4.imprint","INTERSECT",VERTEX,{"derivedFrom":[sQuery(id+"F4.wireOp",EDGE,"E57"),subQ0]});Q2=makeQuery(id+"F4.imprint","IMPRINT",FACE,{"disambiguationData":[TD([[makeQuery(id+"F4.imprint","IMPRINT",EDGE,{"disambiguationData":[TD([[subQ1,1.0]])],"derivedFrom":subQ0}),1.0]])]});}
            var Q3;
            {var subQ0=sQuery(id+"F4.wireOp",EDGE,"E60");var subQ1=makeQuery(id+"F4.imprint","INTERSECT",VERTEX,{"derivedFrom":[sQuery(id+"F4.wireOp",EDGE,"E54"),subQ0]});Q3=makeQuery(id+"F4.imprint","IMPRINT",FACE,{"disambiguationData":[TD([[makeQuery(id+"F4.imprint","IMPRINT",EDGE,{"disambiguationData":[TD([[subQ1,-1.0]])],"derivedFrom":subQ0}),1.0]])]});}
            var Q4;
            {var subQ0=sQuery(id+"F4.wireOp",EDGE,"E58");var subQ1=sQuery(id+"F4.wireOp",EDGE,"E56");var subQ2=makeQuery(id+"F4.imprint","INTERSECT",VERTEX,{"derivedFrom":[subQ1,subQ0]});Q4=makeQuery(id+"F4.imprint","IMPRINT",FACE,{"disambiguationData":[TD([[makeQuery(id+"F4.imprint","IMPRINT",EDGE,{"disambiguationData":[TD([[subQ2,-1.0]])],"derivedFrom":subQ1}),-1.0]])]});}
            var Q5;
            {var subQ0=sQuery(id+"F4.wireOp",EDGE,"E58");var subQ1=makeQuery(id+"F4.imprint","INTERSECT",VERTEX,{"derivedFrom":[sQuery(id+"F4.wireOp",EDGE,"E54"),subQ0]});Q5=makeQuery(id+"F4.imprint","IMPRINT",FACE,{"disambiguationData":[TD([[makeQuery(id+"F4.imprint","IMPRINT",EDGE,{"disambiguationData":[TD([[subQ1,1.0]])],"derivedFrom":subQ0}),1.0]])]});}
            var Q6;
            {var subQ0=sQuery(id+"F4.wireOp",EDGE,"E59");var subQ1=makeQuery(id+"F4.imprint","INTERSECT",VERTEX,{"derivedFrom":[sQuery(id+"F4.wireOp",EDGE,"E55"),subQ0]});Q6=makeQuery(id+"F4.imprint","IMPRINT",FACE,{"disambiguationData":[TD([[makeQuery(id+"F4.imprint","IMPRINT",EDGE,{"disambiguationData":[TD([[subQ1,1.0]])],"derivedFrom":subQ0}),1.0]])]});}
            var Q7;
            {var subQ0=sQuery(id+"F4.wireOp",EDGE,"E60");var subQ1=sQuery(id+"F4.wireOp",EDGE,"E54");var subQ2=makeQuery(id+"F4.imprint","INTERSECT",VERTEX,{"derivedFrom":[subQ1,subQ0]});Q7=makeQuery(id+"F4.imprint","IMPRINT",FACE,{"disambiguationData":[TD([[makeQuery(id+"F4.imprint","IMPRINT",EDGE,{"disambiguationData":[TD([[subQ2,1.0]])],"derivedFrom":subQ0}),-1.0]])]});}
            var Q8;
            {var subQ0=sQuery(id+"F4.wireOp",EDGE,"E61");var subQ1=makeQuery(id+"F4.imprint","INTERSECT",VERTEX,{"derivedFrom":[sQuery(id+"F4.wireOp",EDGE,"E54"),subQ0]});Q8=makeQuery(id+"F4.imprint","IMPRINT",FACE,{"disambiguationData":[TD([[makeQuery(id+"F4.imprint","IMPRINT",EDGE,{"disambiguationData":[TD([[subQ1,1.0]])],"derivedFrom":subQ0}),1.0]])]});}
            extrude(context, id + "F5", {"entities" : qUnion([Q0, Q1, Q2, Q3, Q4, Q5, Q6, Q7, Q8]), "operationType" : NewBodyOperationType.REMOVE, "oppositeDirection" : true, "depth" : 8 * mm, "offsetDistance" : 25 * mm});
        }
    });
